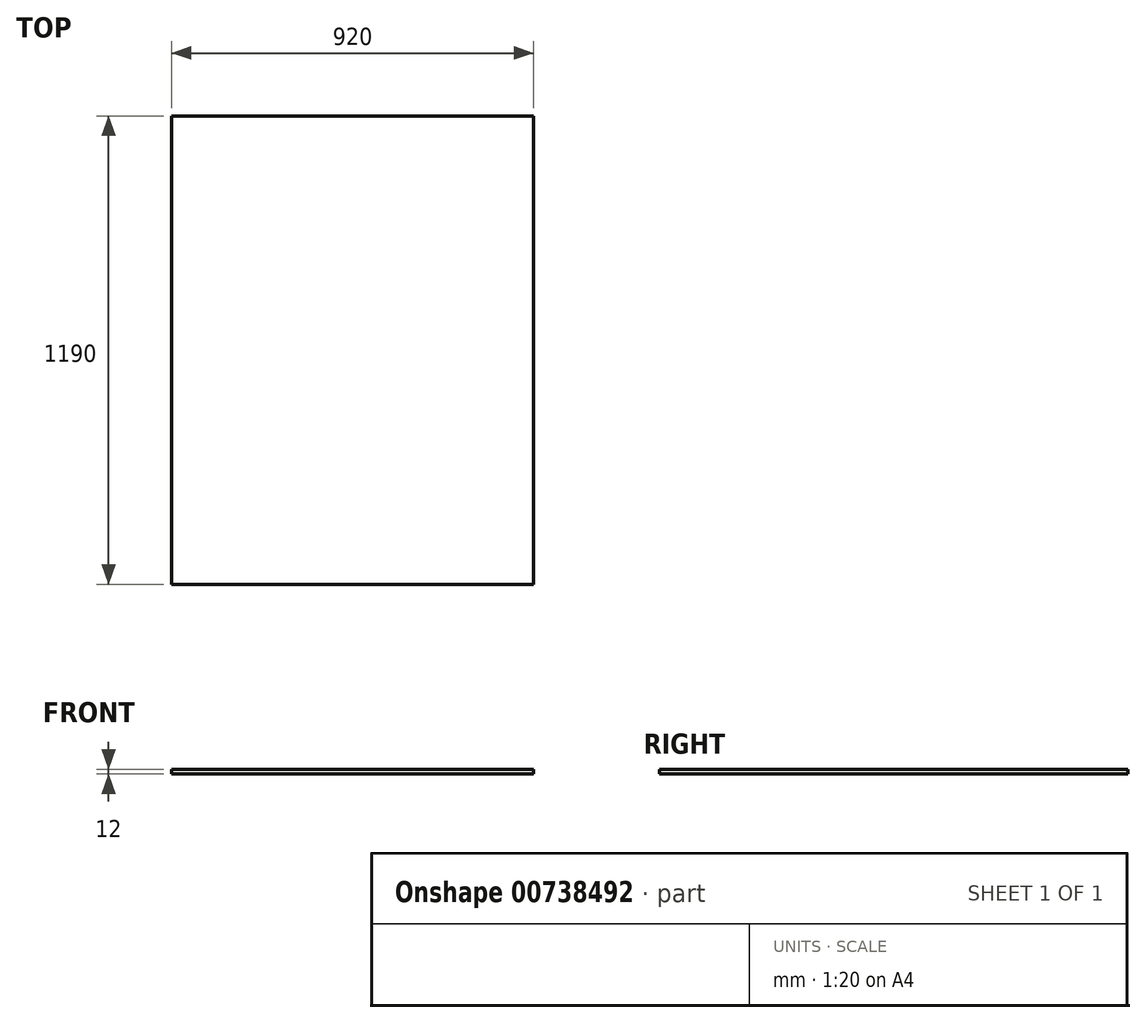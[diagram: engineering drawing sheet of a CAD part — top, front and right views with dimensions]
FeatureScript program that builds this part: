
annotation { "Feature Type Name" : "Feature", "Feature Type Description" : "" }
export const myFeature = defineFeature(function(context is Context, id is Id, definition is map)
    precondition{}
    {
        {
            var Q0;
            Q0=qCreatedBy(makeId("Top.planeOp"),FACE);
            var sketch = newSketch(context, id + "F0", { "sketchPlane" : qUnion([Q0])});
            skLineSegment(sketch, "E0.bottom", {"start": v(460, -595) * mm, "end": v(-460, -595) * mm});
            skLineSegment(sketch, "E0.top", {"start": v(460, 595) * mm, "end": v(-460, 595) * mm});
            skLineSegment(sketch, "E0.left", {"start": v(460, -595) * mm, "end": v(460, 595) * mm});
            skLineSegment(sketch, "E0.right", {"start": v(-460, -595) * mm, "end": v(-460, 595) * mm});
            skPoint(sketch, "E0.middle", {"position": v(0, 0) * mm});
            skSolve(sketch);
        }
        {
            var Q0;
            Q0=makeQuery(id+"F0.imprint","IMPRINT",FACE,{"disambiguationData":[TD([[makeQuery(id+"F0.imprint","IMPRINT",EDGE,{"derivedFrom":sQuery(id+"F0.wireOp",EDGE,"E0.bottom")}),-1.0]])]});
            extrude(context, id + "F1", {"entities" : qUnion([Q0]), "depth" : 12 * mm, "offsetDistance" : 25 * mm});
        }
    });
